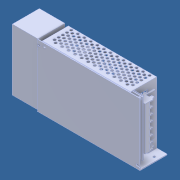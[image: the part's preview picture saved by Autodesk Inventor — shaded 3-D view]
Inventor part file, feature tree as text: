
AUTODESK INVENTOR PART (.ipt)
format: ipt  version: 2018 (Build 220112000, 112)  size: 956,416 bytes
history: native  units: mm
features: other x8, fillet x2, extrude x1, sketch x1
ambient origin geometry x8: Origin, YZ Plane, XZ Plane, XY Plane, X Axis, Y Axis, Z Axis, Center Point
bodies: Solid1 (feature_tree), Solid2 (feature_tree), Solid3 (feature_tree), Solid4 (feature_tree), Solid5 (feature_tree), Solid6 (feature_tree), Solid7 (feature_tree), Solid8 (feature_tree), Solid9 (feature_tree), Solid10 (feature_tree)
feature tree (12):
  extrude  "Extrusion1"  [1 undecoded]
  sketch  "Sketch1"  dims[d0=40.0mm d1=0.0mm]
  other  "Boss-Extrude7"
  other  "LPattern2[1]"
  other  "LPattern2[2]"
  other  "LPattern2[3]"
  other  "LPattern2[4]"
  other  "LPattern2[5]"
  other  "LPattern2[6]"
  other  "Cut-Extrude14[2]"
  fillet  "Fillet9"  [1 undecoded]
  fillet  "Fillet10"  [1 undecoded]
note: 3 required parameter values undecoded (feature->parameter linkage not recoverable at this tier; creation-order binding heuristic only, values carry confidence <= 0.55)
